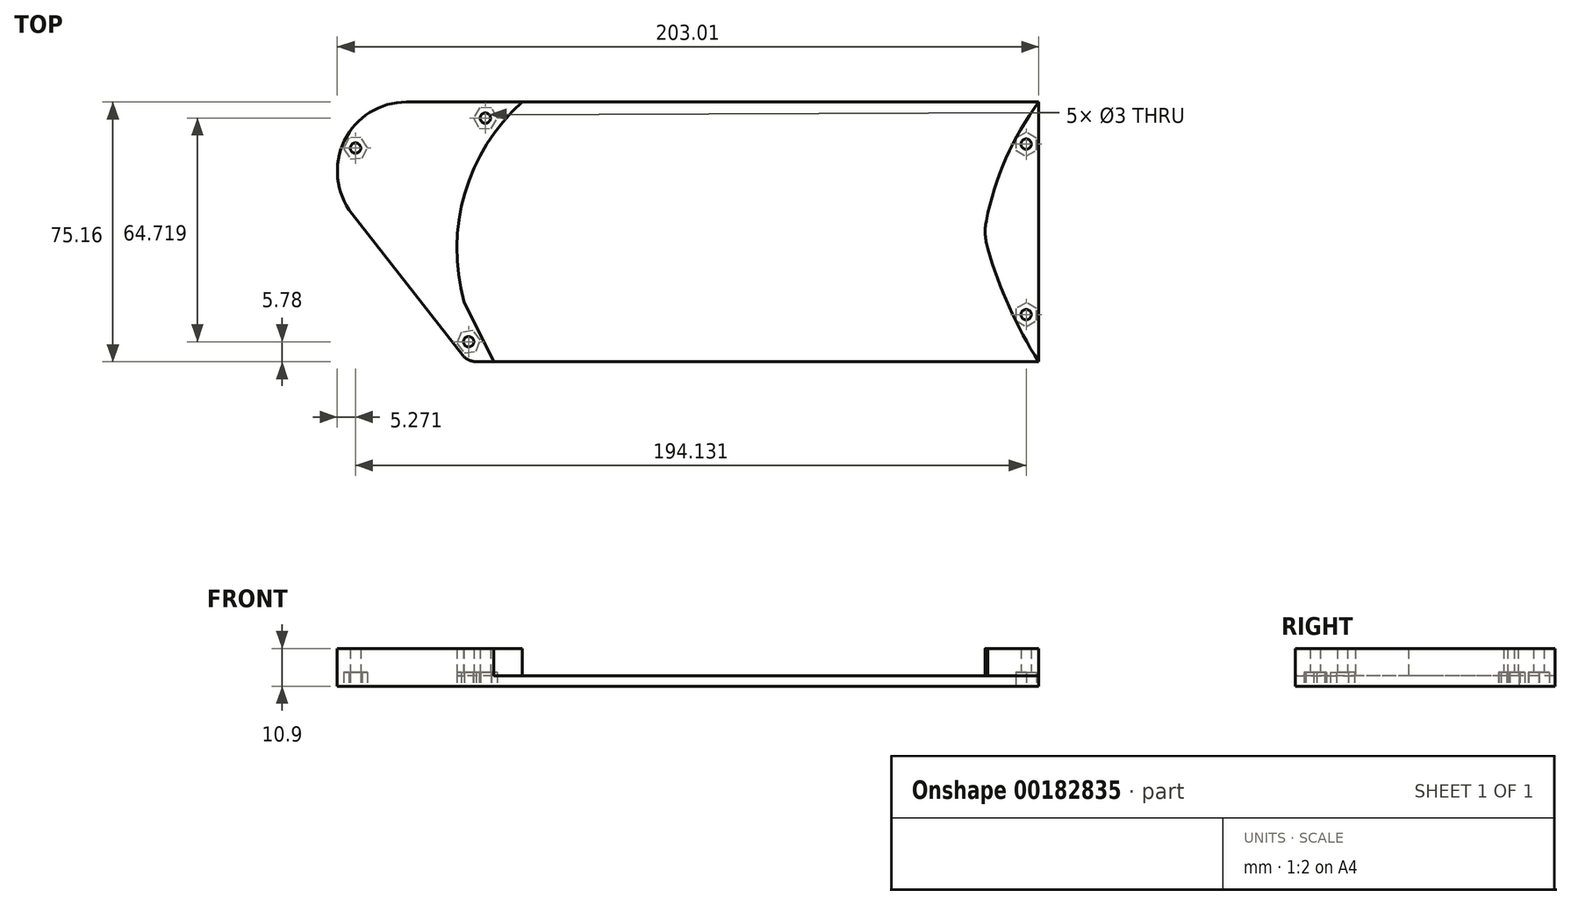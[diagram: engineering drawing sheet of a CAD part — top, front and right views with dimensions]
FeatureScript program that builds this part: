
annotation { "Feature Type Name" : "Feature", "Feature Type Description" : "" }
export const myFeature = defineFeature(function(context is Context, id is Id, definition is map)
    precondition{}
    {
        {
            var Q0;
            Q0=qCreatedBy(makeId("Top.planeOp"),FACE);
            var sketch = newSketch(context, id + "F0", { "sketchPlane" : qUnion([Q0])});
            skLineSegment(sketch, "E0", {"start": v(83.8, 37.87) * mm, "end": v(-99.2, 37.87) * mm});
            skLineSegment(sketch, "E1", {"start": v(83.8, -37.29) * mm, "end": v(-81.47, -37.29) * mm});
            skLineSegment(sketch, "E2.0", {"start": v(83.8, -37.29) * mm, "end": v(83.8, 37.87) * mm});
            skArc(sketch, "E3", {"start": v(68.64, 3.43) * mm, "mid": v(68.35, -0.57) * mm, "end": v(69.09, -4.5) * mm});
            skLineSegment(sketch, "E4", {"start": v(-73.97, -37.29) * mm, "end": v(-82.52, -19.87) * mm});
            skArc(sketch, "E5", {"start": v(-65.62, 37.87) * mm, "mid": v(-82.32, 11.42) * mm, "end": v(-82.52, -19.87) * mm});
            skArc(sketch, "E6", {"start": v(69.09, -4.5) * mm, "mid": v(75.26, -21.43) * mm, "end": v(83.8, -37.29) * mm});
            skLineSegment(sketch, "E7", {"start": v(-81.47, -37.29) * mm, "end": v(-114.97, 5.55) * mm});
            skArc(sketch, "E8", {"start": v(-99.2, 37.87) * mm, "mid": v(-117.19, 26.64) * mm, "end": v(-114.97, 5.55) * mm});
            skArc(sketch, "E9", {"start": v(83.8, 37.87) * mm, "mid": v(74.32, 21.49) * mm, "end": v(68.64, 3.43) * mm});
            skSolve(sketch);
        }
        {
            var Q0;
            Q0=makeQuery(id+"F0.imprint","IMPRINT",FACE,{"disambiguationData":[TD([[makeQuery(id+"F0.imprint","IMPRINT",EDGE,{"derivedFrom":sQuery(id+"F0.wireOp",EDGE,"E3")}),-1.0]])]});
            var sketch = newSketch(context, id + "F1", { "sketchPlane" : qUnion([Q0])});
            skSolve(sketch);
        }
        {
            var Q0;
            Q0=qSketchRegion(id+"F1",true);
            var Q1;
            Q1=makeQuery(id+"F0.imprint","IMPRINT",FACE,{"disambiguationData":[TD([[makeQuery(id+"F0.imprint","IMPRINT",EDGE,{"derivedFrom":sQuery(id+"F0.wireOp",EDGE,"E3")}),-1.0]])]});
            extrude(context, id + "F2", {"entities" : qUnion([Q0, Q1]), "oppositeDirection" : true, "depth" : 3 * mm});
        }
        {
            var Q0;
            {var subQ3=sQuery(id+"F0.wireOp",EDGE,"E4");Q0=makeQuery(id+"F0.imprint","IMPRINT",FACE,{"disambiguationData":[TD([[makeQuery(id+"F0.imprint","IMPRINT",EDGE,{"derivedFrom":subQ3}),1.0]])]});}
            extrude(context, id + "F3", {"entities" : qUnion([Q0]), "depth" : 7.9 * mm});
        }
        {
            var Q0;
            {var subQ0=sQuery(id+"F0.wireOp",EDGE,"E2.0");Q0=makeQuery(id+"F0.imprint","IMPRINT",FACE,{"disambiguationData":[TD([[makeQuery(id+"F0.imprint","IMPRINT",EDGE,{"derivedFrom":subQ0}),1.0]])]});}
            extrude(context, id + "F4", {"entities" : qUnion([Q0]), "depth" : 7.9 * mm});
        }
        {
            var Q0;
            Q0=makeQuery(id+"F3.opExtrude","CAP_FACE",FACE,{"disambiguationData":[OSD([sQuery(id+"F0.wireOp",EDGE,"E0"),sQuery(id+"F0.wireOp",EDGE,"E1"),sQuery(id+"F0.wireOp",EDGE,"E4"),sQuery(id+"F0.wireOp",EDGE,"E5"),sQuery(id+"F0.wireOp",EDGE,"lp4rXHfa-9uQE-Nh6Z-oIaG-cHkOYRsXJNMD"),sQuery(id+"F0.wireOp",EDGE,"E7"),sQuery(id+"F0.wireOp",EDGE,"E8")])],"isStart":true});
            var Q1;
            Q1=makeQuery(id+"F4.opExtrude","CAP_FACE",FACE,{"disambiguationData":[OSD([sQuery(id+"F0.wireOp",EDGE,"E0"),sQuery(id+"F0.wireOp",EDGE,"E1"),sQuery(id+"F0.wireOp",EDGE,"E2.0"),sQuery(id+"F0.wireOp",EDGE,"E3"),sQuery(id+"F0.wireOp",EDGE,"uJdoGhJC-Amh7-iMku-Pf1O-IdhWUITwSaAr"),sQuery(id+"F0.wireOp",EDGE,"E6")])],"isStart":true});
            extrude(context, id + "F5", {"entities" : qUnion([Q0, Q1]), "depth" : 3 * mm});
        }
        {
            var Q0;
            Q0=makeQuery(id+"F3.opExtrude","SWEPT_EDGE",EDGE,{"disambiguationData":[OSD([sQuery(id+"F0.wireOp",EDGE,"E1"),sQuery(id+"F0.wireOp",EDGE,"E7")])]});
            var Q1;
            Q1=makeQuery(id+"F5.opExtrude","SWEPT_EDGE",EDGE,{"disambiguationData":[OSD([sQuery(id+"F0.wireOp",EDGE,"E1"),sQuery(id+"F0.wireOp",EDGE,"E7")])]});
            fillet(context, id + "F6", {"entities" : qUnion([Q0, Q1]), "radius" : 5 * mm, "tangentPropagation" : true, "allowEdgeOverflow" : false});
        }
        {
            var Q0;
            Q0=makeQuery(id+"F2.opExtrude","SWEPT_BODY",BODY,{"disambiguationData":[OSD([sQuery(id+"F0.wireOp",EDGE,"E0"),sQuery(id+"F0.wireOp",EDGE,"E1"),sQuery(id+"F0.wireOp",EDGE,"E3"),sQuery(id+"F0.wireOp",EDGE,"E4"),sQuery(id+"F0.wireOp",EDGE,"E5"),sQuery(id+"F0.wireOp",EDGE,"E6"),sQuery(id+"F0.wireOp",EDGE,"E9")])]});
            var Q1;
            Q1=makeQuery(id+"F3.opExtrude","SWEPT_BODY",BODY,{"disambiguationData":[OSD([sQuery(id+"F0.wireOp",EDGE,"E0"),sQuery(id+"F0.wireOp",EDGE,"E1"),sQuery(id+"F0.wireOp",EDGE,"E4"),sQuery(id+"F0.wireOp",EDGE,"E5"),sQuery(id+"F0.wireOp",EDGE,"lp4rXHfa-9uQE-Nh6Z-oIaG-cHkOYRsXJNMD"),sQuery(id+"F0.wireOp",EDGE,"E7"),sQuery(id+"F0.wireOp",EDGE,"E8")])]});
            var Q2;
            Q2=makeQuery(id+"F4.opExtrude","SWEPT_BODY",BODY,{"disambiguationData":[OSD([sQuery(id+"F0.wireOp",EDGE,"E2.0"),sQuery(id+"F0.wireOp",EDGE,"E3"),sQuery(id+"F0.wireOp",EDGE,"E6"),sQuery(id+"F0.wireOp",EDGE,"E9")])]});
            var Q3;
            Q3=makeQuery(id+"F5.opExtrude","SWEPT_BODY",BODY,{"disambiguationData":[OSD([sQuery(id+"F0.wireOp",EDGE,"E0"),sQuery(id+"F0.wireOp",EDGE,"E1"),sQuery(id+"F0.wireOp",EDGE,"E4"),sQuery(id+"F0.wireOp",EDGE,"E5"),sQuery(id+"F0.wireOp",EDGE,"lp4rXHfa-9uQE-Nh6Z-oIaG-cHkOYRsXJNMD"),sQuery(id+"F0.wireOp",EDGE,"E7"),sQuery(id+"F0.wireOp",EDGE,"E8")])]});
            var Q4;
            Q4=makeQuery(id+"F5.opExtrude","SWEPT_BODY",BODY,{"disambiguationData":[OSD([sQuery(id+"F0.wireOp",EDGE,"E2.0"),sQuery(id+"F0.wireOp",EDGE,"E3"),sQuery(id+"F0.wireOp",EDGE,"E6"),sQuery(id+"F0.wireOp",EDGE,"E9")])]});
            booleanBodies(context, id + "F7", {"operationType" : BooleanOperationType.UNION, "tools" : qUnion([Q0, Q1, Q2, Q3, Q4])});
        }
        {
            var Q0;
            {var subQ0=sQuery(id+"F0.wireOp",EDGE,"E5");var subQ1=sQuery(id+"F0.wireOp",EDGE,"E4");var subQ2=sQuery(id+"F0.wireOp",EDGE,"E1");var subQ3=sQuery(id+"F0.wireOp",EDGE,"E0");var subQ4=sQuery(id+"F0.wireOp",EDGE,"E9");var subQ5=sQuery(id+"F0.wireOp",EDGE,"E6");var subQ6=sQuery(id+"F0.wireOp",EDGE,"E3");Q0=makeQuery(id+"F7.opBoolean","MERGE",FACE,{"derivedFrom":[makeQuery(id+"F2.opExtrude","CAP_FACE",FACE,{"disambiguationData":[OSD([subQ3,subQ2,subQ6,subQ1,subQ0,subQ5,subQ4])],"isStart":false}),makeQuery(id+"F5.opExtrude","CAP_FACE",FACE,{"disambiguationData":[OSD([sQuery(id+"F0.wireOp",EDGE,"E2.0"),subQ6,subQ5,subQ4])],"isStart":false}),makeQuery(id+"F5.opExtrude","CAP_FACE",FACE,{"disambiguationData":[OSD([subQ3,subQ2,subQ1,subQ0,sQuery(id+"F0.wireOp",EDGE,"lp4rXHfa-9uQE-Nh6Z-oIaG-cHkOYRsXJNMD"),sQuery(id+"F0.wireOp",EDGE,"E7"),sQuery(id+"F0.wireOp",EDGE,"E8")])],"isStart":false})]});}
            var sketch = newSketch(context, id + "F8", { "sketchPlane" : qUnion([Q0])});
            skPoint(sketch, "E10", {"position": v(-81.19, 31.5) * mm});
            skPoint(sketch, "E11", {"position": v(-76.36, -33.2) * mm});
            skPoint(sketch, "E12", {"position": v(-113.94, -24.55) * mm});
            skCircle(sketch, "E13.cCircle", {"center": v(-76.36, -33.2) * mm, "radius": 3 * mm, "construction": true});
            skLineSegment(sketch, "E13.0", {"start": v(-72.9, -33.15) * mm, "end": v(-74.57, -36.18) * mm});
            skLineSegment(sketch, "E13.1", {"start": v(-74.57, -36.18) * mm, "end": v(-78.04, -36.24) * mm});
            skLineSegment(sketch, "E13.2", {"start": v(-78.04, -36.24) * mm, "end": v(-79.82, -33.27) * mm});
            skLineSegment(sketch, "E13.3", {"start": v(-79.82, -33.27) * mm, "end": v(-78.14, -30.24) * mm});
            skLineSegment(sketch, "E13.4", {"start": v(-78.14, -30.24) * mm, "end": v(-74.67, -30.18) * mm});
            skLineSegment(sketch, "E13.5", {"start": v(-74.67, -30.18) * mm, "end": v(-72.9, -33.15) * mm});
            skPoint(sketch, "E13.0.midPoint", {"position": v(-73.73, -34.67) * mm});
            skPoint(sketch, "E14", {"position": v(80.2, 23.66) * mm});
            skPoint(sketch, "E15", {"position": v(80.2, -25.7) * mm});
            skCircle(sketch, "E16.cCircle", {"center": v(80.2, 23.66) * mm, "radius": 3 * mm, "construction": true});
            skLineSegment(sketch, "E16.0", {"start": v(83.2, 25.4) * mm, "end": v(83.2, 21.93) * mm});
            skLineSegment(sketch, "E16.1", {"start": v(83.2, 21.93) * mm, "end": v(80.2, 20.2) * mm});
            skLineSegment(sketch, "E16.2", {"start": v(80.2, 20.2) * mm, "end": v(77.2, 21.93) * mm});
            skLineSegment(sketch, "E16.3", {"start": v(77.2, 21.93) * mm, "end": v(77.2, 25.4) * mm});
            skLineSegment(sketch, "E16.4", {"start": v(77.2, 25.4) * mm, "end": v(80.2, 27.13) * mm});
            skLineSegment(sketch, "E16.5", {"start": v(80.2, 27.13) * mm, "end": v(83.2, 25.4) * mm});
            skPoint(sketch, "E16.0.midPoint", {"position": v(83.2, 23.66) * mm});
            skCircle(sketch, "E17.cCircle", {"center": v(80.2, -25.7) * mm, "radius": 3 * mm, "construction": true});
            skLineSegment(sketch, "E17.0", {"start": v(83.2, -23.97) * mm, "end": v(83.2, -27.43) * mm});
            skLineSegment(sketch, "E17.1", {"start": v(83.2, -27.43) * mm, "end": v(80.2, -29.16) * mm});
            skLineSegment(sketch, "E17.2", {"start": v(80.2, -29.16) * mm, "end": v(77.2, -27.43) * mm});
            skLineSegment(sketch, "E17.3", {"start": v(77.2, -27.43) * mm, "end": v(77.2, -23.97) * mm});
            skLineSegment(sketch, "E17.4", {"start": v(77.2, -23.97) * mm, "end": v(80.2, -22.24) * mm});
            skLineSegment(sketch, "E17.5", {"start": v(80.2, -22.24) * mm, "end": v(83.2, -23.97) * mm});
            skPoint(sketch, "E17.0.midPoint", {"position": v(83.2, -25.7) * mm});
            skCircle(sketch, "E18.cCircle", {"center": v(-81.19, 31.5) * mm, "radius": 3 * mm, "construction": true});
            skLineSegment(sketch, "E18.0", {"start": v(-77.76, 31.04) * mm, "end": v(-79.88, 28.3) * mm});
            skLineSegment(sketch, "E18.1", {"start": v(-79.88, 28.3) * mm, "end": v(-83.3, 28.77) * mm});
            skLineSegment(sketch, "E18.2", {"start": v(-83.3, 28.77) * mm, "end": v(-84.62, 31.98) * mm});
            skLineSegment(sketch, "E18.3", {"start": v(-84.62, 31.98) * mm, "end": v(-82.5, 34.72) * mm});
            skLineSegment(sketch, "E18.4", {"start": v(-82.5, 34.72) * mm, "end": v(-79.07, 34.25) * mm});
            skLineSegment(sketch, "E18.5", {"start": v(-79.07, 34.25) * mm, "end": v(-77.76, 31.04) * mm});
            skPoint(sketch, "E18.0.midPoint", {"position": v(-78.82, 29.67) * mm});
            skCircle(sketch, "E19.cCircle", {"center": v(-113.94, -24.55) * mm, "radius": 3 * mm, "construction": true});
            skLineSegment(sketch, "E19.0", {"start": v(-112.04, -21.66) * mm, "end": v(-110.48, -24.76) * mm});
            skLineSegment(sketch, "E19.1", {"start": v(-110.48, -24.76) * mm, "end": v(-112.38, -27.65) * mm});
            skLineSegment(sketch, "E19.2", {"start": v(-112.38, -27.65) * mm, "end": v(-115.84, -27.45) * mm});
            skLineSegment(sketch, "E19.3", {"start": v(-115.84, -27.45) * mm, "end": v(-117.4, -24.35) * mm});
            skLineSegment(sketch, "E19.4", {"start": v(-117.4, -24.35) * mm, "end": v(-115.5, -21.46) * mm});
            skLineSegment(sketch, "E19.5", {"start": v(-115.5, -21.46) * mm, "end": v(-112.04, -21.66) * mm});
            skPoint(sketch, "E19.0.midPoint", {"position": v(-111.26, -23.2) * mm});
            skSolve(sketch);
        }
        {
            var Q0;
            Q0=sQuery(id+"F8.wireOp",VERTEX,"E10");
            var Q1;
            Q1=sQuery(id+"F8.wireOp",VERTEX,"E12");
            var Q2;
            Q2=sQuery(id+"F8.wireOp",VERTEX,"E11");
            var Q3;
            Q3=sQuery(id+"F8.wireOp",VERTEX,"E14");
            var Q4;
            Q4=sQuery(id+"F8.wireOp",VERTEX,"E15");
            var Q5;
            Q5=makeQuery(id+"F2.opExtrude","SWEPT_BODY",BODY,{"disambiguationData":[OSD([sQuery(id+"F0.wireOp",EDGE,"E0"),sQuery(id+"F0.wireOp",EDGE,"E1"),sQuery(id+"F0.wireOp",EDGE,"E3"),sQuery(id+"F0.wireOp",EDGE,"E4"),sQuery(id+"F0.wireOp",EDGE,"E5"),sQuery(id+"F0.wireOp",EDGE,"E6"),sQuery(id+"F0.wireOp",EDGE,"E9")])]});
            hole(context, id + "F9", {"style" : HoleStyle.SIMPLE, "endStyle" : HoleEndStyle.THROUGH, "holeDiameter" : 3 * mm, "startFromSketch" : true, "locations" : qUnion([Q0, Q1, Q2, Q3, Q4]), "scope" : qUnion([Q5]), "isTappedThrough" : true});
        }
        {
            var Q0;
            Q0=qSketchRegion(id+"F8",true);
            extrude(context, id + "F10", {"entities" : qUnion([Q0]), "operationType" : NewBodyOperationType.REMOVE, "oppositeDirection" : true, "depth" : 4 * mm});
        }
        {
            var Q0;
            Q0=qSketchRegion(id+"F8",true);
            extrude(context, id + "F11", {"entities" : qUnion([Q0]), "operationType" : NewBodyOperationType.REMOVE, "oppositeDirection" : true, "depth" : 4 * mm});
        }
    });
